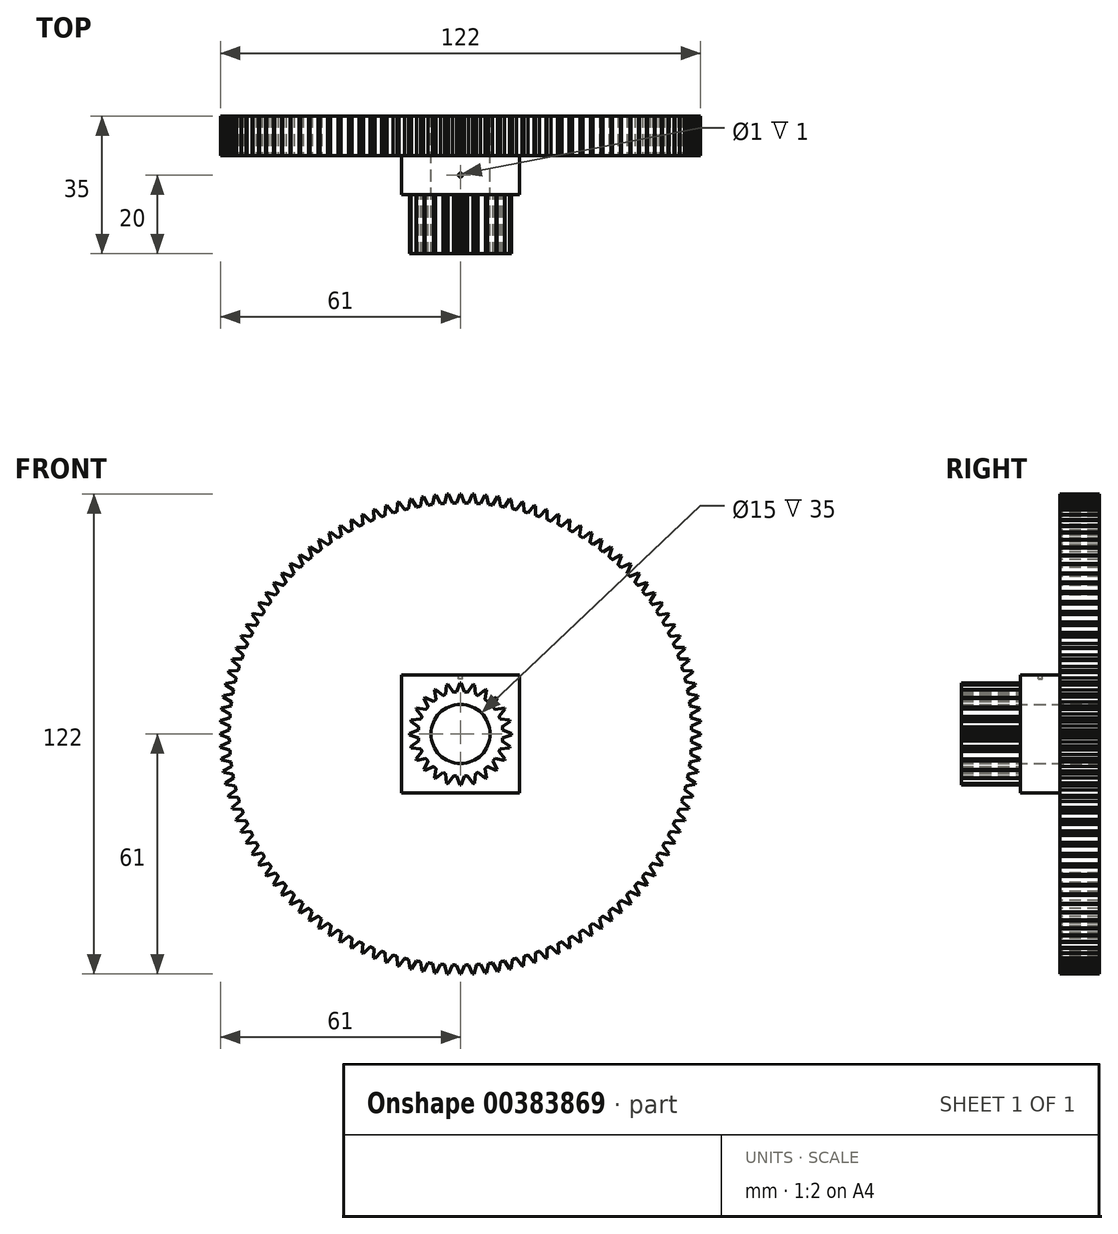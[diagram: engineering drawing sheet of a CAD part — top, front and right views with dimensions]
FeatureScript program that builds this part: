
annotation { "Feature Type Name" : "Feature", "Feature Type Description" : "" }
export const myFeature = defineFeature(function(context is Context, id is Id, definition is map)
    precondition{}
    {
        {
            var Q0;
            Q0=qCreatedBy(makeId("Front.planeOp"),FACE);
            var sketch = newSketch(context, id + "F0", { "sketchPlane" : qUnion([Q0])});
            skCircle(sketch, "E0", {"center": v(0, 0) * mm, "radius": 7.5 * mm});
            skCircle(sketch, "E1", {"center": v(0, 0) * mm, "radius": 10.75 * mm});
            skCircle(sketch, "E2", {"center": v(0, 0) * mm, "radius": 13 * mm, "construction": true});
            skLineSegment(sketch, "E3", {"start": v(-1.02, 10.7) * mm, "end": v(-0.19, 13) * mm});
            skLineSegment(sketch, "E4", {"start": v(-0.19, 13) * mm, "end": v(0, 13) * mm});
            skLineSegment(sketch, "E5", {"start": v(-1.02, 10.7) * mm, "end": v(-1.02, 13.91) * mm, "construction": true});
            skLineSegment(sketch, "E6.MirrorCS", {"start": v(0.19, 13) * mm, "end": v(0, 13) * mm});
            skLineSegment(sketch, "E7.MirrorCS", {"start": v(1.02, 10.7) * mm, "end": v(0.19, 13) * mm});
            skLineSegment(sketch, "E8.1.0", {"start": v(-3.76, 10.07) * mm, "end": v(-3.55, 12.5) * mm});
            skLineSegment(sketch, "E8.1.1", {"start": v(-3.55, 12.5) * mm, "end": v(-3.36, 12.56) * mm});
            skLineSegment(sketch, "E8.1.2", {"start": v(-3.18, 12.6) * mm, "end": v(-3.36, 12.56) * mm});
            skLineSegment(sketch, "E8.1.3", {"start": v(-1.78, 10.6) * mm, "end": v(-3.18, 12.6) * mm});
            skLineSegment(sketch, "E8.2.0", {"start": v(-6.24, 8.76) * mm, "end": v(-6.66, 11.16) * mm});
            skLineSegment(sketch, "E8.2.1", {"start": v(-6.66, 11.16) * mm, "end": v(-6.5, 11.26) * mm});
            skLineSegment(sketch, "E8.2.2", {"start": v(-6.34, 11.35) * mm, "end": v(-6.5, 11.26) * mm});
            skLineSegment(sketch, "E8.2.3", {"start": v(-4.46, 9.78) * mm, "end": v(-6.34, 11.35) * mm});
            skLineSegment(sketch, "E8.3.0", {"start": v(-8.3, 6.84) * mm, "end": v(-9.32, 9.06) * mm});
            skLineSegment(sketch, "E8.3.1", {"start": v(-9.32, 9.06) * mm, "end": v(-9.2, 9.2) * mm});
            skLineSegment(sketch, "E8.3.2", {"start": v(-9.06, 9.32) * mm, "end": v(-9.2, 9.2) * mm});
            skLineSegment(sketch, "E8.3.3", {"start": v(-6.84, 8.3) * mm, "end": v(-9.06, 9.32) * mm});
            skLineSegment(sketch, "E8.4.0", {"start": v(-9.78, 4.46) * mm, "end": v(-11.35, 6.34) * mm});
            skLineSegment(sketch, "E8.4.1", {"start": v(-11.35, 6.34) * mm, "end": v(-11.26, 6.5) * mm});
            skLineSegment(sketch, "E8.4.2", {"start": v(-11.16, 6.66) * mm, "end": v(-11.26, 6.5) * mm});
            skLineSegment(sketch, "E8.4.3", {"start": v(-8.76, 6.24) * mm, "end": v(-11.16, 6.66) * mm});
            skLineSegment(sketch, "E8.5.0", {"start": v(-10.6, 1.78) * mm, "end": v(-12.6, 3.18) * mm});
            skLineSegment(sketch, "E8.5.1", {"start": v(-12.6, 3.18) * mm, "end": v(-12.56, 3.36) * mm});
            skLineSegment(sketch, "E8.5.2", {"start": v(-12.5, 3.55) * mm, "end": v(-12.56, 3.36) * mm});
            skLineSegment(sketch, "E8.5.3", {"start": v(-10.07, 3.76) * mm, "end": v(-12.5, 3.55) * mm});
            skLineSegment(sketch, "E8.6.0", {"start": v(-10.7, -1.02) * mm, "end": v(-13, -0.19) * mm});
            skLineSegment(sketch, "E8.6.1", {"start": v(-13, -0.19) * mm, "end": v(-13, 0) * mm});
            skLineSegment(sketch, "E8.6.2", {"start": v(-13, 0.19) * mm, "end": v(-13, 0) * mm});
            skLineSegment(sketch, "E8.6.3", {"start": v(-10.7, 1.02) * mm, "end": v(-13, 0.19) * mm});
            skLineSegment(sketch, "E8.7.0", {"start": v(-10.07, -3.76) * mm, "end": v(-12.5, -3.55) * mm});
            skLineSegment(sketch, "E8.7.1", {"start": v(-12.5, -3.55) * mm, "end": v(-12.56, -3.36) * mm});
            skLineSegment(sketch, "E8.7.2", {"start": v(-12.6, -3.18) * mm, "end": v(-12.56, -3.36) * mm});
            skLineSegment(sketch, "E8.7.3", {"start": v(-10.6, -1.78) * mm, "end": v(-12.6, -3.18) * mm});
            skLineSegment(sketch, "E8.8.0", {"start": v(-8.76, -6.24) * mm, "end": v(-11.16, -6.66) * mm});
            skLineSegment(sketch, "E8.8.1", {"start": v(-11.16, -6.66) * mm, "end": v(-11.26, -6.5) * mm});
            skLineSegment(sketch, "E8.8.2", {"start": v(-11.35, -6.34) * mm, "end": v(-11.26, -6.5) * mm});
            skLineSegment(sketch, "E8.8.3", {"start": v(-9.78, -4.46) * mm, "end": v(-11.35, -6.34) * mm});
            skLineSegment(sketch, "E8.9.0", {"start": v(-6.84, -8.3) * mm, "end": v(-9.06, -9.32) * mm});
            skLineSegment(sketch, "E8.9.1", {"start": v(-9.06, -9.32) * mm, "end": v(-9.2, -9.2) * mm});
            skLineSegment(sketch, "E8.9.2", {"start": v(-9.32, -9.06) * mm, "end": v(-9.2, -9.2) * mm});
            skLineSegment(sketch, "E8.9.3", {"start": v(-8.3, -6.84) * mm, "end": v(-9.32, -9.06) * mm});
            skLineSegment(sketch, "E8.10.0", {"start": v(-4.46, -9.78) * mm, "end": v(-6.34, -11.35) * mm});
            skLineSegment(sketch, "E8.10.1", {"start": v(-6.34, -11.35) * mm, "end": v(-6.5, -11.26) * mm});
            skLineSegment(sketch, "E8.10.2", {"start": v(-6.66, -11.16) * mm, "end": v(-6.5, -11.26) * mm});
            skLineSegment(sketch, "E8.10.3", {"start": v(-6.24, -8.76) * mm, "end": v(-6.66, -11.16) * mm});
            skLineSegment(sketch, "E8.11.0", {"start": v(-1.78, -10.6) * mm, "end": v(-3.18, -12.6) * mm});
            skLineSegment(sketch, "E8.11.1", {"start": v(-3.18, -12.6) * mm, "end": v(-3.36, -12.56) * mm});
            skLineSegment(sketch, "E8.11.2", {"start": v(-3.55, -12.5) * mm, "end": v(-3.36, -12.56) * mm});
            skLineSegment(sketch, "E8.11.3", {"start": v(-3.76, -10.07) * mm, "end": v(-3.55, -12.5) * mm});
            skLineSegment(sketch, "E9.1.12.0", {"start": v(1.02, -10.7) * mm, "end": v(0.19, -13) * mm});
            skLineSegment(sketch, "E9.3.12.0", {"start": v(0.19, -13) * mm, "end": v(0, -13) * mm});
            skLineSegment(sketch, "E9.6.12.0", {"start": v(-0.19, -13) * mm, "end": v(0, -13) * mm});
            skLineSegment(sketch, "E9.9.12.0", {"start": v(-1.02, -10.7) * mm, "end": v(-0.19, -13) * mm});
            skLineSegment(sketch, "E9.1.13.0", {"start": v(3.76, -10.07) * mm, "end": v(3.55, -12.5) * mm});
            skLineSegment(sketch, "E9.3.13.0", {"start": v(3.55, -12.5) * mm, "end": v(3.36, -12.56) * mm});
            skLineSegment(sketch, "E9.6.13.0", {"start": v(3.18, -12.6) * mm, "end": v(3.36, -12.56) * mm});
            skLineSegment(sketch, "E9.9.13.0", {"start": v(1.78, -10.6) * mm, "end": v(3.18, -12.6) * mm});
            skLineSegment(sketch, "E9.1.14.0", {"start": v(6.24, -8.76) * mm, "end": v(6.66, -11.16) * mm});
            skLineSegment(sketch, "E9.3.14.0", {"start": v(6.66, -11.16) * mm, "end": v(6.5, -11.26) * mm});
            skLineSegment(sketch, "E9.6.14.0", {"start": v(6.34, -11.35) * mm, "end": v(6.5, -11.26) * mm});
            skLineSegment(sketch, "E9.9.14.0", {"start": v(4.46, -9.78) * mm, "end": v(6.34, -11.35) * mm});
            skLineSegment(sketch, "E9.1.15.0", {"start": v(8.3, -6.84) * mm, "end": v(9.32, -9.06) * mm});
            skLineSegment(sketch, "E9.3.15.0", {"start": v(9.32, -9.06) * mm, "end": v(9.2, -9.2) * mm});
            skLineSegment(sketch, "E9.6.15.0", {"start": v(9.06, -9.32) * mm, "end": v(9.2, -9.2) * mm});
            skLineSegment(sketch, "E9.9.15.0", {"start": v(6.84, -8.3) * mm, "end": v(9.06, -9.32) * mm});
            skLineSegment(sketch, "E9.1.16.0", {"start": v(9.78, -4.46) * mm, "end": v(11.35, -6.34) * mm});
            skLineSegment(sketch, "E9.3.16.0", {"start": v(11.35, -6.34) * mm, "end": v(11.26, -6.5) * mm});
            skLineSegment(sketch, "E9.6.16.0", {"start": v(11.16, -6.66) * mm, "end": v(11.26, -6.5) * mm});
            skLineSegment(sketch, "E9.9.16.0", {"start": v(8.76, -6.24) * mm, "end": v(11.16, -6.66) * mm});
            skLineSegment(sketch, "E9.1.17.0", {"start": v(10.6, -1.78) * mm, "end": v(12.6, -3.18) * mm});
            skLineSegment(sketch, "E9.3.17.0", {"start": v(12.6, -3.18) * mm, "end": v(12.56, -3.36) * mm});
            skLineSegment(sketch, "E9.6.17.0", {"start": v(12.5, -3.55) * mm, "end": v(12.56, -3.36) * mm});
            skLineSegment(sketch, "E9.9.17.0", {"start": v(10.07, -3.76) * mm, "end": v(12.5, -3.55) * mm});
            skLineSegment(sketch, "E9.1.18.0", {"start": v(10.7, 1.02) * mm, "end": v(13, 0.19) * mm});
            skLineSegment(sketch, "E9.3.18.0", {"start": v(13, 0.19) * mm, "end": v(13, 0) * mm});
            skLineSegment(sketch, "E9.6.18.0", {"start": v(13, -0.19) * mm, "end": v(13, 0) * mm});
            skLineSegment(sketch, "E9.9.18.0", {"start": v(10.7, -1.02) * mm, "end": v(13, -0.19) * mm});
            skLineSegment(sketch, "E9.1.19.0", {"start": v(10.07, 3.76) * mm, "end": v(12.5, 3.55) * mm});
            skLineSegment(sketch, "E9.3.19.0", {"start": v(12.5, 3.55) * mm, "end": v(12.56, 3.36) * mm});
            skLineSegment(sketch, "E9.6.19.0", {"start": v(12.6, 3.18) * mm, "end": v(12.56, 3.36) * mm});
            skLineSegment(sketch, "E9.9.19.0", {"start": v(10.6, 1.78) * mm, "end": v(12.6, 3.18) * mm});
            skLineSegment(sketch, "E9.1.20.0", {"start": v(8.76, 6.24) * mm, "end": v(11.16, 6.66) * mm});
            skLineSegment(sketch, "E9.3.20.0", {"start": v(11.16, 6.66) * mm, "end": v(11.26, 6.5) * mm});
            skLineSegment(sketch, "E9.6.20.0", {"start": v(11.35, 6.34) * mm, "end": v(11.26, 6.5) * mm});
            skLineSegment(sketch, "E9.9.20.0", {"start": v(9.78, 4.46) * mm, "end": v(11.35, 6.34) * mm});
            skLineSegment(sketch, "E9.1.21.0", {"start": v(6.84, 8.3) * mm, "end": v(9.06, 9.32) * mm});
            skLineSegment(sketch, "E9.3.21.0", {"start": v(9.06, 9.32) * mm, "end": v(9.2, 9.2) * mm});
            skLineSegment(sketch, "E9.6.21.0", {"start": v(9.32, 9.06) * mm, "end": v(9.2, 9.2) * mm});
            skLineSegment(sketch, "E9.9.21.0", {"start": v(8.3, 6.84) * mm, "end": v(9.32, 9.06) * mm});
            skLineSegment(sketch, "E9.1.22.0", {"start": v(4.46, 9.78) * mm, "end": v(6.34, 11.35) * mm});
            skLineSegment(sketch, "E9.3.22.0", {"start": v(6.34, 11.35) * mm, "end": v(6.5, 11.26) * mm});
            skLineSegment(sketch, "E9.6.22.0", {"start": v(6.66, 11.16) * mm, "end": v(6.5, 11.26) * mm});
            skLineSegment(sketch, "E9.9.22.0", {"start": v(6.24, 8.76) * mm, "end": v(6.66, 11.16) * mm});
            skLineSegment(sketch, "E9.1.23.0", {"start": v(1.78, 10.6) * mm, "end": v(3.18, 12.6) * mm});
            skLineSegment(sketch, "E9.3.23.0", {"start": v(3.18, 12.6) * mm, "end": v(3.36, 12.56) * mm});
            skLineSegment(sketch, "E9.6.23.0", {"start": v(3.55, 12.5) * mm, "end": v(3.36, 12.56) * mm});
            skLineSegment(sketch, "E9.9.23.0", {"start": v(3.76, 10.07) * mm, "end": v(3.55, 12.5) * mm});
            skSolve(sketch);
        }
        {
            var Q0;
            Q0=qSketchRegion(id+"F0",true);
            extrude(context, id + "F1", {"entities" : qUnion([Q0]), "depth" : 15 * mm});
        }
        {
            var Q0;
            Q0=qCreatedBy(makeId("Front.planeOp"),FACE);
            var sketch = newSketch(context, id + "F2", { "sketchPlane" : qUnion([Q0])});
            skCircle(sketch, "E10", {"center": v(0, 0) * mm, "radius": 7.5 * mm});
            skLineSegment(sketch, "E11.bottom", {"start": v(-15, -15) * mm, "end": v(15, -15) * mm});
            skLineSegment(sketch, "E11.top", {"start": v(-15, 15) * mm, "end": v(15, 15) * mm});
            skLineSegment(sketch, "E11.left", {"start": v(-15, -15) * mm, "end": v(-15, 15) * mm});
            skLineSegment(sketch, "E11.right", {"start": v(15, -15) * mm, "end": v(15, 15) * mm});
            skSolve(sketch);
        }
        {
            var Q0;
            Q0 = qSketchRegion(id + "F2", true);
            extrude(context, id + "F3", {"entities" : qUnion([Q0]), "operationType" : NewBodyOperationType.ADD, "depth" : -10 * mm});
        }
        {
            var Q0;
            Q0=makeQuery(id+"F3.opExtrude","CAP_FACE",FACE,{"disambiguationData":[OSD([sQuery(id+"F2.wireOp",EDGE,"Zh5lLQ9h-1iR5-KiPg-C2Wr-JR3NM9Zv75rL"),sQuery(id+"F2.wireOp",EDGE,"E10")])],"isStart":false});
            var sketch = newSketch(context, id + "F4", { "sketchPlane" : qUnion([Q0])});
            skCircle(sketch, "E12", {"center": v(0, 0) * mm, "radius": 58.75 * mm});
            skCircle(sketch, "E13", {"center": v(0, 0) * mm, "radius": 61 * mm, "construction": true});
            skLineSegment(sketch, "E14", {"start": v(-1, 58.74) * mm, "end": v(-1, 64.16) * mm, "construction": true});
            skLineSegment(sketch, "E15", {"start": v(-1, 58.74) * mm, "end": v(-0.19, 61) * mm});
            skLineSegment(sketch, "E16", {"start": v(-0.19, 61) * mm, "end": v(0, 61) * mm});
            skLineSegment(sketch, "E17.MirrorCS", {"start": v(0.19, 61) * mm, "end": v(0, 61) * mm});
            skLineSegment(sketch, "E18.MirrorCS", {"start": v(1, 58.74) * mm, "end": v(0.19, 61) * mm});
            skLineSegment(sketch, "E19.1.0", {"start": v(-4.08, 58.6) * mm, "end": v(-3.38, 60.9) * mm});
            skLineSegment(sketch, "E19.1.1", {"start": v(-3.38, 60.9) * mm, "end": v(-3.2, 60.92) * mm});
            skLineSegment(sketch, "E19.1.2", {"start": v(-3, 60.93) * mm, "end": v(-3.2, 60.92) * mm});
            skLineSegment(sketch, "E19.1.3", {"start": v(-2.07, 58.71) * mm, "end": v(-3, 60.93) * mm});
            skLineSegment(sketch, "E19.2.0", {"start": v(-7.14, 58.31) * mm, "end": v(-6.56, 60.65) * mm});
            skLineSegment(sketch, "E19.2.1", {"start": v(-6.56, 60.65) * mm, "end": v(-6.38, 60.67) * mm});
            skLineSegment(sketch, "E19.2.2", {"start": v(-6.19, 60.69) * mm, "end": v(-6.38, 60.67) * mm});
            skLineSegment(sketch, "E19.2.3", {"start": v(-5.14, 58.53) * mm, "end": v(-6.19, 60.69) * mm});
            skLineSegment(sketch, "E19.3.0", {"start": v(-10.19, 57.86) * mm, "end": v(-9.73, 60.22) * mm});
            skLineSegment(sketch, "E19.3.1", {"start": v(-9.73, 60.22) * mm, "end": v(-9.54, 60.25) * mm});
            skLineSegment(sketch, "E19.3.2", {"start": v(-9.36, 60.28) * mm, "end": v(-9.54, 60.25) * mm});
            skLineSegment(sketch, "E19.3.3", {"start": v(-8.2, 58.18) * mm, "end": v(-9.36, 60.28) * mm});
            skLineSegment(sketch, "E19.4.0", {"start": v(-13.2, 57.25) * mm, "end": v(-12.87, 59.63) * mm});
            skLineSegment(sketch, "E19.4.1", {"start": v(-12.87, 59.63) * mm, "end": v(-12.68, 59.67) * mm});
            skLineSegment(sketch, "E19.4.2", {"start": v(-12.5, 59.7) * mm, "end": v(-12.68, 59.67) * mm});
            skLineSegment(sketch, "E19.4.3", {"start": v(-11.23, 57.67) * mm, "end": v(-12.5, 59.7) * mm});
            skLineSegment(sketch, "E19.5.0", {"start": v(-16.18, 56.48) * mm, "end": v(-15.97, 58.87) * mm});
            skLineSegment(sketch, "E19.5.1", {"start": v(-15.97, 58.87) * mm, "end": v(-15.79, 58.92) * mm});
            skLineSegment(sketch, "E19.5.2", {"start": v(-15.6, 58.97) * mm, "end": v(-15.79, 58.92) * mm});
            skLineSegment(sketch, "E19.5.3", {"start": v(-14.23, 57) * mm, "end": v(-15.6, 58.97) * mm});
            skLineSegment(sketch, "E19.6.0", {"start": v(-19.11, 55.55) * mm, "end": v(-19.03, 57.96) * mm});
            skLineSegment(sketch, "E19.6.1", {"start": v(-19.03, 57.96) * mm, "end": v(-18.85, 58.01) * mm});
            skLineSegment(sketch, "E19.6.2", {"start": v(-18.67, 58.07) * mm, "end": v(-18.85, 58.01) * mm});
            skLineSegment(sketch, "E19.6.3", {"start": v(-17.2, 56.18) * mm, "end": v(-18.67, 58.07) * mm});
            skLineSegment(sketch, "E19.7.0", {"start": v(-22, 54.48) * mm, "end": v(-22.04, 56.88) * mm});
            skLineSegment(sketch, "E19.7.1", {"start": v(-22.04, 56.88) * mm, "end": v(-21.86, 56.95) * mm});
            skLineSegment(sketch, "E19.7.2", {"start": v(-21.69, 57.02) * mm, "end": v(-21.86, 56.95) * mm});
            skLineSegment(sketch, "E19.7.3", {"start": v(-20.1, 55.2) * mm, "end": v(-21.69, 57.02) * mm});
            skLineSegment(sketch, "E19.8.0", {"start": v(-24.81, 53.25) * mm, "end": v(-24.98, 55.65) * mm});
            skLineSegment(sketch, "E19.8.1", {"start": v(-24.98, 55.65) * mm, "end": v(-24.81, 55.73) * mm});
            skLineSegment(sketch, "E19.8.2", {"start": v(-24.64, 55.8) * mm, "end": v(-24.81, 55.73) * mm});
            skLineSegment(sketch, "E19.8.3", {"start": v(-22.97, 54.07) * mm, "end": v(-24.64, 55.8) * mm});
            skLineSegment(sketch, "E19.9.0", {"start": v(-27.57, 51.88) * mm, "end": v(-27.86, 54.27) * mm});
            skLineSegment(sketch, "E19.9.1", {"start": v(-27.86, 54.27) * mm, "end": v(-27.7, 54.35) * mm});
            skLineSegment(sketch, "E19.9.2", {"start": v(-27.53, 54.44) * mm, "end": v(-27.7, 54.35) * mm});
            skLineSegment(sketch, "E19.9.3", {"start": v(-25.77, 52.8) * mm, "end": v(-27.53, 54.44) * mm});
            skLineSegment(sketch, "E19.10.0", {"start": v(-30.24, 50.37) * mm, "end": v(-30.66, 52.73) * mm});
            skLineSegment(sketch, "E19.10.1", {"start": v(-30.66, 52.73) * mm, "end": v(-30.5, 52.83) * mm});
            skLineSegment(sketch, "E19.10.2", {"start": v(-30.34, 52.92) * mm, "end": v(-30.5, 52.83) * mm});
            skLineSegment(sketch, "E19.10.3", {"start": v(-28.5, 51.38) * mm, "end": v(-30.34, 52.92) * mm});
            skLineSegment(sketch, "E19.11.0", {"start": v(-32.84, 48.71) * mm, "end": v(-33.38, 51.06) * mm});
            skLineSegment(sketch, "E19.11.1", {"start": v(-33.38, 51.06) * mm, "end": v(-33.22, 51.16) * mm});
            skLineSegment(sketch, "E19.11.2", {"start": v(-33.07, 51.26) * mm, "end": v(-33.22, 51.16) * mm});
            skLineSegment(sketch, "E19.11.3", {"start": v(-31.15, 49.81) * mm, "end": v(-33.07, 51.26) * mm});
            skLineSegment(sketch, "E19.12.0", {"start": v(-35.34, 46.93) * mm, "end": v(-36, 49.24) * mm});
            skLineSegment(sketch, "E19.12.1", {"start": v(-36, 49.24) * mm, "end": v(-35.85, 49.35) * mm});
            skLineSegment(sketch, "E19.12.2", {"start": v(-35.7, 49.46) * mm, "end": v(-35.85, 49.35) * mm});
            skLineSegment(sketch, "E19.12.3", {"start": v(-33.71, 48.12) * mm, "end": v(-35.7, 49.46) * mm});
            skLineSegment(sketch, "E19.13.0", {"start": v(-37.75, 45.02) * mm, "end": v(-38.53, 47.29) * mm});
            skLineSegment(sketch, "E19.13.1", {"start": v(-38.53, 47.29) * mm, "end": v(-38.39, 47.4) * mm});
            skLineSegment(sketch, "E19.13.2", {"start": v(-38.24, 47.52) * mm, "end": v(-38.39, 47.4) * mm});
            skLineSegment(sketch, "E19.13.3", {"start": v(-36.18, 46.29) * mm, "end": v(-38.24, 47.52) * mm});
            skLineSegment(sketch, "E19.14.0", {"start": v(-40.06, 42.98) * mm, "end": v(-40.96, 45.2) * mm});
            skLineSegment(sketch, "E19.14.1", {"start": v(-40.96, 45.2) * mm, "end": v(-40.82, 45.33) * mm});
            skLineSegment(sketch, "E19.14.2", {"start": v(-40.68, 45.46) * mm, "end": v(-40.82, 45.33) * mm});
            skLineSegment(sketch, "E19.14.3", {"start": v(-38.56, 44.33) * mm, "end": v(-40.68, 45.46) * mm});
            skLineSegment(sketch, "E19.15.0", {"start": v(-42.25, 40.82) * mm, "end": v(-43.27, 43) * mm});
            skLineSegment(sketch, "E19.15.1", {"start": v(-43.27, 43) * mm, "end": v(-43.13, 43.13) * mm});
            skLineSegment(sketch, "E19.15.2", {"start": v(-43, 43.27) * mm, "end": v(-43.13, 43.13) * mm});
            skLineSegment(sketch, "E19.15.3", {"start": v(-40.82, 42.25) * mm, "end": v(-43, 43.27) * mm});
            skLineSegment(sketch, "E19.16.0", {"start": v(-44.33, 38.56) * mm, "end": v(-45.46, 40.68) * mm});
            skLineSegment(sketch, "E19.16.1", {"start": v(-45.46, 40.68) * mm, "end": v(-45.33, 40.82) * mm});
            skLineSegment(sketch, "E19.16.2", {"start": v(-45.2, 40.96) * mm, "end": v(-45.33, 40.82) * mm});
            skLineSegment(sketch, "E19.16.3", {"start": v(-42.98, 40.06) * mm, "end": v(-45.2, 40.96) * mm});
            skLineSegment(sketch, "E19.17.0", {"start": v(-46.29, 36.18) * mm, "end": v(-47.52, 38.24) * mm});
            skLineSegment(sketch, "E19.17.1", {"start": v(-47.52, 38.24) * mm, "end": v(-47.4, 38.39) * mm});
            skLineSegment(sketch, "E19.17.2", {"start": v(-47.29, 38.53) * mm, "end": v(-47.4, 38.39) * mm});
            skLineSegment(sketch, "E19.17.3", {"start": v(-45.02, 37.75) * mm, "end": v(-47.29, 38.53) * mm});
            skLineSegment(sketch, "E19.18.0", {"start": v(-48.12, 33.71) * mm, "end": v(-49.46, 35.7) * mm});
            skLineSegment(sketch, "E19.18.1", {"start": v(-49.46, 35.7) * mm, "end": v(-49.35, 35.85) * mm});
            skLineSegment(sketch, "E19.18.2", {"start": v(-49.24, 36) * mm, "end": v(-49.35, 35.85) * mm});
            skLineSegment(sketch, "E19.18.3", {"start": v(-46.93, 35.34) * mm, "end": v(-49.24, 36) * mm});
            skLineSegment(sketch, "E19.19.0", {"start": v(-49.81, 31.15) * mm, "end": v(-51.26, 33.07) * mm});
            skLineSegment(sketch, "E19.19.1", {"start": v(-51.26, 33.07) * mm, "end": v(-51.16, 33.22) * mm});
            skLineSegment(sketch, "E19.19.2", {"start": v(-51.06, 33.38) * mm, "end": v(-51.16, 33.22) * mm});
            skLineSegment(sketch, "E19.19.3", {"start": v(-48.71, 32.84) * mm, "end": v(-51.06, 33.38) * mm});
            skLineSegment(sketch, "E19.20.0", {"start": v(-51.38, 28.5) * mm, "end": v(-52.92, 30.34) * mm});
            skLineSegment(sketch, "E19.20.1", {"start": v(-52.92, 30.34) * mm, "end": v(-52.83, 30.5) * mm});
            skLineSegment(sketch, "E19.20.2", {"start": v(-52.73, 30.66) * mm, "end": v(-52.83, 30.5) * mm});
            skLineSegment(sketch, "E19.20.3", {"start": v(-50.37, 30.24) * mm, "end": v(-52.73, 30.66) * mm});
            skLineSegment(sketch, "E19.21.0", {"start": v(-52.8, 25.77) * mm, "end": v(-54.44, 27.53) * mm});
            skLineSegment(sketch, "E19.21.1", {"start": v(-54.44, 27.53) * mm, "end": v(-54.35, 27.7) * mm});
            skLineSegment(sketch, "E19.21.2", {"start": v(-54.27, 27.86) * mm, "end": v(-54.35, 27.7) * mm});
            skLineSegment(sketch, "E19.21.3", {"start": v(-51.88, 27.57) * mm, "end": v(-54.27, 27.86) * mm});
            skLineSegment(sketch, "E19.22.0", {"start": v(-54.07, 22.97) * mm, "end": v(-55.8, 24.64) * mm});
            skLineSegment(sketch, "E19.22.1", {"start": v(-55.8, 24.64) * mm, "end": v(-55.73, 24.81) * mm});
            skLineSegment(sketch, "E19.22.2", {"start": v(-55.65, 24.98) * mm, "end": v(-55.73, 24.81) * mm});
            skLineSegment(sketch, "E19.22.3", {"start": v(-53.25, 24.81) * mm, "end": v(-55.65, 24.98) * mm});
            skLineSegment(sketch, "E19.23.0", {"start": v(-55.2, 20.1) * mm, "end": v(-57.02, 21.69) * mm});
            skLineSegment(sketch, "E19.23.1", {"start": v(-57.02, 21.69) * mm, "end": v(-56.95, 21.86) * mm});
            skLineSegment(sketch, "E19.23.2", {"start": v(-56.88, 22.04) * mm, "end": v(-56.95, 21.86) * mm});
            skLineSegment(sketch, "E19.23.3", {"start": v(-54.48, 22) * mm, "end": v(-56.88, 22.04) * mm});
            skLineSegment(sketch, "E19.24.0", {"start": v(-56.18, 17.2) * mm, "end": v(-58.07, 18.67) * mm});
            skLineSegment(sketch, "E19.24.1", {"start": v(-58.07, 18.67) * mm, "end": v(-58.01, 18.85) * mm});
            skLineSegment(sketch, "E19.24.2", {"start": v(-57.96, 19.03) * mm, "end": v(-58.01, 18.85) * mm});
            skLineSegment(sketch, "E19.24.3", {"start": v(-55.55, 19.11) * mm, "end": v(-57.96, 19.03) * mm});
            skLineSegment(sketch, "E19.25.0", {"start": v(-57, 14.23) * mm, "end": v(-58.97, 15.6) * mm});
            skLineSegment(sketch, "E19.25.1", {"start": v(-58.97, 15.6) * mm, "end": v(-58.92, 15.79) * mm});
            skLineSegment(sketch, "E19.25.2", {"start": v(-58.87, 15.97) * mm, "end": v(-58.92, 15.79) * mm});
            skLineSegment(sketch, "E19.25.3", {"start": v(-56.48, 16.18) * mm, "end": v(-58.87, 15.97) * mm});
            skLineSegment(sketch, "E19.26.0", {"start": v(-57.67, 11.23) * mm, "end": v(-59.7, 12.5) * mm});
            skLineSegment(sketch, "E19.26.1", {"start": v(-59.7, 12.5) * mm, "end": v(-59.67, 12.68) * mm});
            skLineSegment(sketch, "E19.26.2", {"start": v(-59.63, 12.87) * mm, "end": v(-59.67, 12.68) * mm});
            skLineSegment(sketch, "E19.26.3", {"start": v(-57.25, 13.2) * mm, "end": v(-59.63, 12.87) * mm});
            skLineSegment(sketch, "E19.27.0", {"start": v(-58.18, 8.2) * mm, "end": v(-60.28, 9.36) * mm});
            skLineSegment(sketch, "E19.27.1", {"start": v(-60.28, 9.36) * mm, "end": v(-60.25, 9.54) * mm});
            skLineSegment(sketch, "E19.27.2", {"start": v(-60.22, 9.73) * mm, "end": v(-60.25, 9.54) * mm});
            skLineSegment(sketch, "E19.27.3", {"start": v(-57.86, 10.19) * mm, "end": v(-60.22, 9.73) * mm});
            skLineSegment(sketch, "E19.28.0", {"start": v(-58.53, 5.14) * mm, "end": v(-60.69, 6.19) * mm});
            skLineSegment(sketch, "E19.28.1", {"start": v(-60.69, 6.19) * mm, "end": v(-60.67, 6.38) * mm});
            skLineSegment(sketch, "E19.28.2", {"start": v(-60.65, 6.56) * mm, "end": v(-60.67, 6.38) * mm});
            skLineSegment(sketch, "E19.28.3", {"start": v(-58.31, 7.14) * mm, "end": v(-60.65, 6.56) * mm});
            skLineSegment(sketch, "E19.29.0", {"start": v(-58.71, 2.07) * mm, "end": v(-60.93, 3) * mm});
            skLineSegment(sketch, "E19.29.1", {"start": v(-60.93, 3) * mm, "end": v(-60.92, 3.2) * mm});
            skLineSegment(sketch, "E19.29.2", {"start": v(-60.9, 3.38) * mm, "end": v(-60.92, 3.2) * mm});
            skLineSegment(sketch, "E19.29.3", {"start": v(-58.6, 4.08) * mm, "end": v(-60.9, 3.38) * mm});
            skLineSegment(sketch, "E19.30.0", {"start": v(-58.74, -1) * mm, "end": v(-61, -0.19) * mm});
            skLineSegment(sketch, "E19.30.1", {"start": v(-61, -0.19) * mm, "end": v(-61, 0) * mm});
            skLineSegment(sketch, "E19.30.2", {"start": v(-61, 0.19) * mm, "end": v(-61, 0) * mm});
            skLineSegment(sketch, "E19.30.3", {"start": v(-58.74, 1) * mm, "end": v(-61, 0.19) * mm});
            skLineSegment(sketch, "E19.31.0", {"start": v(-58.6, -4.08) * mm, "end": v(-60.9, -3.38) * mm});
            skLineSegment(sketch, "E19.31.1", {"start": v(-60.9, -3.38) * mm, "end": v(-60.92, -3.2) * mm});
            skLineSegment(sketch, "E19.31.2", {"start": v(-60.93, -3) * mm, "end": v(-60.92, -3.2) * mm});
            skLineSegment(sketch, "E19.31.3", {"start": v(-58.71, -2.07) * mm, "end": v(-60.93, -3) * mm});
            skLineSegment(sketch, "E19.32.0", {"start": v(-58.31, -7.14) * mm, "end": v(-60.65, -6.56) * mm});
            skLineSegment(sketch, "E19.32.1", {"start": v(-60.65, -6.56) * mm, "end": v(-60.67, -6.38) * mm});
            skLineSegment(sketch, "E19.32.2", {"start": v(-60.69, -6.19) * mm, "end": v(-60.67, -6.38) * mm});
            skLineSegment(sketch, "E19.32.3", {"start": v(-58.53, -5.14) * mm, "end": v(-60.69, -6.19) * mm});
            skLineSegment(sketch, "E19.33.0", {"start": v(-57.86, -10.19) * mm, "end": v(-60.22, -9.73) * mm});
            skLineSegment(sketch, "E19.33.1", {"start": v(-60.22, -9.73) * mm, "end": v(-60.25, -9.54) * mm});
            skLineSegment(sketch, "E19.33.2", {"start": v(-60.28, -9.36) * mm, "end": v(-60.25, -9.54) * mm});
            skLineSegment(sketch, "E19.33.3", {"start": v(-58.18, -8.2) * mm, "end": v(-60.28, -9.36) * mm});
            skLineSegment(sketch, "E19.34.0", {"start": v(-57.25, -13.2) * mm, "end": v(-59.63, -12.87) * mm});
            skLineSegment(sketch, "E19.34.1", {"start": v(-59.63, -12.87) * mm, "end": v(-59.67, -12.68) * mm});
            skLineSegment(sketch, "E19.34.2", {"start": v(-59.7, -12.5) * mm, "end": v(-59.67, -12.68) * mm});
            skLineSegment(sketch, "E19.34.3", {"start": v(-57.67, -11.23) * mm, "end": v(-59.7, -12.5) * mm});
            skLineSegment(sketch, "E19.35.0", {"start": v(-56.48, -16.18) * mm, "end": v(-58.87, -15.97) * mm});
            skLineSegment(sketch, "E19.35.1", {"start": v(-58.87, -15.97) * mm, "end": v(-58.92, -15.79) * mm});
            skLineSegment(sketch, "E19.35.2", {"start": v(-58.97, -15.6) * mm, "end": v(-58.92, -15.79) * mm});
            skLineSegment(sketch, "E19.35.3", {"start": v(-57, -14.23) * mm, "end": v(-58.97, -15.6) * mm});
            skLineSegment(sketch, "E19.36.0", {"start": v(-55.55, -19.11) * mm, "end": v(-57.96, -19.03) * mm});
            skLineSegment(sketch, "E19.36.1", {"start": v(-57.96, -19.03) * mm, "end": v(-58.01, -18.85) * mm});
            skLineSegment(sketch, "E19.36.2", {"start": v(-58.07, -18.67) * mm, "end": v(-58.01, -18.85) * mm});
            skLineSegment(sketch, "E19.36.3", {"start": v(-56.18, -17.2) * mm, "end": v(-58.07, -18.67) * mm});
            skLineSegment(sketch, "E19.37.0", {"start": v(-54.48, -22) * mm, "end": v(-56.88, -22.04) * mm});
            skLineSegment(sketch, "E19.37.1", {"start": v(-56.88, -22.04) * mm, "end": v(-56.95, -21.86) * mm});
            skLineSegment(sketch, "E19.37.2", {"start": v(-57.02, -21.69) * mm, "end": v(-56.95, -21.86) * mm});
            skLineSegment(sketch, "E19.37.3", {"start": v(-55.2, -20.1) * mm, "end": v(-57.02, -21.69) * mm});
            skLineSegment(sketch, "E19.38.0", {"start": v(-53.25, -24.81) * mm, "end": v(-55.65, -24.98) * mm});
            skLineSegment(sketch, "E19.38.1", {"start": v(-55.65, -24.98) * mm, "end": v(-55.73, -24.81) * mm});
            skLineSegment(sketch, "E19.38.2", {"start": v(-55.8, -24.64) * mm, "end": v(-55.73, -24.81) * mm});
            skLineSegment(sketch, "E19.38.3", {"start": v(-54.07, -22.97) * mm, "end": v(-55.8, -24.64) * mm});
            skLineSegment(sketch, "E19.39.0", {"start": v(-51.88, -27.57) * mm, "end": v(-54.27, -27.86) * mm});
            skLineSegment(sketch, "E19.39.1", {"start": v(-54.27, -27.86) * mm, "end": v(-54.35, -27.7) * mm});
            skLineSegment(sketch, "E19.39.2", {"start": v(-54.44, -27.53) * mm, "end": v(-54.35, -27.7) * mm});
            skLineSegment(sketch, "E19.39.3", {"start": v(-52.8, -25.77) * mm, "end": v(-54.44, -27.53) * mm});
            skLineSegment(sketch, "E19.40.0", {"start": v(-50.37, -30.24) * mm, "end": v(-52.73, -30.66) * mm});
            skLineSegment(sketch, "E19.40.1", {"start": v(-52.73, -30.66) * mm, "end": v(-52.83, -30.5) * mm});
            skLineSegment(sketch, "E19.40.2", {"start": v(-52.92, -30.34) * mm, "end": v(-52.83, -30.5) * mm});
            skLineSegment(sketch, "E19.40.3", {"start": v(-51.38, -28.5) * mm, "end": v(-52.92, -30.34) * mm});
            skLineSegment(sketch, "E19.41.0", {"start": v(-48.71, -32.84) * mm, "end": v(-51.06, -33.38) * mm});
            skLineSegment(sketch, "E19.41.1", {"start": v(-51.06, -33.38) * mm, "end": v(-51.16, -33.22) * mm});
            skLineSegment(sketch, "E19.41.2", {"start": v(-51.26, -33.07) * mm, "end": v(-51.16, -33.22) * mm});
            skLineSegment(sketch, "E19.41.3", {"start": v(-49.81, -31.15) * mm, "end": v(-51.26, -33.07) * mm});
            skLineSegment(sketch, "E19.42.0", {"start": v(-46.93, -35.34) * mm, "end": v(-49.24, -36) * mm});
            skLineSegment(sketch, "E19.42.1", {"start": v(-49.24, -36) * mm, "end": v(-49.35, -35.85) * mm});
            skLineSegment(sketch, "E19.42.2", {"start": v(-49.46, -35.7) * mm, "end": v(-49.35, -35.85) * mm});
            skLineSegment(sketch, "E19.42.3", {"start": v(-48.12, -33.71) * mm, "end": v(-49.46, -35.7) * mm});
            skLineSegment(sketch, "E19.43.0", {"start": v(-45.02, -37.75) * mm, "end": v(-47.29, -38.53) * mm});
            skLineSegment(sketch, "E19.43.1", {"start": v(-47.29, -38.53) * mm, "end": v(-47.4, -38.39) * mm});
            skLineSegment(sketch, "E19.43.2", {"start": v(-47.52, -38.24) * mm, "end": v(-47.4, -38.39) * mm});
            skLineSegment(sketch, "E19.43.3", {"start": v(-46.29, -36.18) * mm, "end": v(-47.52, -38.24) * mm});
            skLineSegment(sketch, "E19.44.0", {"start": v(-42.98, -40.06) * mm, "end": v(-45.2, -40.96) * mm});
            skLineSegment(sketch, "E19.44.1", {"start": v(-45.2, -40.96) * mm, "end": v(-45.33, -40.82) * mm});
            skLineSegment(sketch, "E19.44.2", {"start": v(-45.46, -40.68) * mm, "end": v(-45.33, -40.82) * mm});
            skLineSegment(sketch, "E19.44.3", {"start": v(-44.33, -38.56) * mm, "end": v(-45.46, -40.68) * mm});
            skLineSegment(sketch, "E19.45.0", {"start": v(-40.82, -42.25) * mm, "end": v(-43, -43.27) * mm});
            skLineSegment(sketch, "E19.45.1", {"start": v(-43, -43.27) * mm, "end": v(-43.13, -43.13) * mm});
            skLineSegment(sketch, "E19.45.2", {"start": v(-43.27, -43) * mm, "end": v(-43.13, -43.13) * mm});
            skLineSegment(sketch, "E19.45.3", {"start": v(-42.25, -40.82) * mm, "end": v(-43.27, -43) * mm});
            skLineSegment(sketch, "E19.46.0", {"start": v(-38.56, -44.33) * mm, "end": v(-40.68, -45.46) * mm});
            skLineSegment(sketch, "E19.46.1", {"start": v(-40.68, -45.46) * mm, "end": v(-40.82, -45.33) * mm});
            skLineSegment(sketch, "E19.46.2", {"start": v(-40.96, -45.2) * mm, "end": v(-40.82, -45.33) * mm});
            skLineSegment(sketch, "E19.46.3", {"start": v(-40.06, -42.98) * mm, "end": v(-40.96, -45.2) * mm});
            skLineSegment(sketch, "E19.47.0", {"start": v(-36.18, -46.29) * mm, "end": v(-38.24, -47.52) * mm});
            skLineSegment(sketch, "E19.47.1", {"start": v(-38.24, -47.52) * mm, "end": v(-38.39, -47.4) * mm});
            skLineSegment(sketch, "E19.47.2", {"start": v(-38.53, -47.29) * mm, "end": v(-38.39, -47.4) * mm});
            skLineSegment(sketch, "E19.47.3", {"start": v(-37.75, -45.02) * mm, "end": v(-38.53, -47.29) * mm});
            skLineSegment(sketch, "E19.48.0", {"start": v(-33.71, -48.12) * mm, "end": v(-35.7, -49.46) * mm});
            skLineSegment(sketch, "E19.48.1", {"start": v(-35.7, -49.46) * mm, "end": v(-35.85, -49.35) * mm});
            skLineSegment(sketch, "E19.48.2", {"start": v(-36, -49.24) * mm, "end": v(-35.85, -49.35) * mm});
            skLineSegment(sketch, "E19.48.3", {"start": v(-35.34, -46.93) * mm, "end": v(-36, -49.24) * mm});
            skLineSegment(sketch, "E19.49.0", {"start": v(-31.15, -49.81) * mm, "end": v(-33.07, -51.26) * mm});
            skLineSegment(sketch, "E19.49.1", {"start": v(-33.07, -51.26) * mm, "end": v(-33.22, -51.16) * mm});
            skLineSegment(sketch, "E19.49.2", {"start": v(-33.38, -51.06) * mm, "end": v(-33.22, -51.16) * mm});
            skLineSegment(sketch, "E19.49.3", {"start": v(-32.84, -48.71) * mm, "end": v(-33.38, -51.06) * mm});
            skLineSegment(sketch, "E19.50.0", {"start": v(-28.5, -51.38) * mm, "end": v(-30.34, -52.92) * mm});
            skLineSegment(sketch, "E19.50.1", {"start": v(-30.34, -52.92) * mm, "end": v(-30.5, -52.83) * mm});
            skLineSegment(sketch, "E19.50.2", {"start": v(-30.66, -52.73) * mm, "end": v(-30.5, -52.83) * mm});
            skLineSegment(sketch, "E19.50.3", {"start": v(-30.24, -50.37) * mm, "end": v(-30.66, -52.73) * mm});
            skLineSegment(sketch, "E19.51.0", {"start": v(-25.77, -52.8) * mm, "end": v(-27.53, -54.44) * mm});
            skLineSegment(sketch, "E19.51.1", {"start": v(-27.53, -54.44) * mm, "end": v(-27.7, -54.35) * mm});
            skLineSegment(sketch, "E19.51.2", {"start": v(-27.86, -54.27) * mm, "end": v(-27.7, -54.35) * mm});
            skLineSegment(sketch, "E19.51.3", {"start": v(-27.57, -51.88) * mm, "end": v(-27.86, -54.27) * mm});
            skLineSegment(sketch, "E19.52.0", {"start": v(-22.97, -54.07) * mm, "end": v(-24.64, -55.8) * mm});
            skLineSegment(sketch, "E19.52.1", {"start": v(-24.64, -55.8) * mm, "end": v(-24.81, -55.73) * mm});
            skLineSegment(sketch, "E19.52.2", {"start": v(-24.98, -55.65) * mm, "end": v(-24.81, -55.73) * mm});
            skLineSegment(sketch, "E19.52.3", {"start": v(-24.81, -53.25) * mm, "end": v(-24.98, -55.65) * mm});
            skLineSegment(sketch, "E19.53.0", {"start": v(-20.1, -55.2) * mm, "end": v(-21.69, -57.02) * mm});
            skLineSegment(sketch, "E19.53.1", {"start": v(-21.69, -57.02) * mm, "end": v(-21.86, -56.95) * mm});
            skLineSegment(sketch, "E19.53.2", {"start": v(-22.04, -56.88) * mm, "end": v(-21.86, -56.95) * mm});
            skLineSegment(sketch, "E19.53.3", {"start": v(-22, -54.48) * mm, "end": v(-22.04, -56.88) * mm});
            skLineSegment(sketch, "E19.54.0", {"start": v(-17.2, -56.18) * mm, "end": v(-18.67, -58.07) * mm});
            skLineSegment(sketch, "E19.54.1", {"start": v(-18.67, -58.07) * mm, "end": v(-18.85, -58.01) * mm});
            skLineSegment(sketch, "E19.54.2", {"start": v(-19.03, -57.96) * mm, "end": v(-18.85, -58.01) * mm});
            skLineSegment(sketch, "E19.54.3", {"start": v(-19.11, -55.55) * mm, "end": v(-19.03, -57.96) * mm});
            skLineSegment(sketch, "E19.55.0", {"start": v(-14.23, -57) * mm, "end": v(-15.6, -58.97) * mm});
            skLineSegment(sketch, "E19.55.1", {"start": v(-15.6, -58.97) * mm, "end": v(-15.79, -58.92) * mm});
            skLineSegment(sketch, "E19.55.2", {"start": v(-15.97, -58.87) * mm, "end": v(-15.79, -58.92) * mm});
            skLineSegment(sketch, "E19.55.3", {"start": v(-16.18, -56.48) * mm, "end": v(-15.97, -58.87) * mm});
            skLineSegment(sketch, "E19.56.0", {"start": v(-11.23, -57.67) * mm, "end": v(-12.5, -59.7) * mm});
            skLineSegment(sketch, "E19.56.1", {"start": v(-12.5, -59.7) * mm, "end": v(-12.68, -59.67) * mm});
            skLineSegment(sketch, "E19.56.2", {"start": v(-12.87, -59.63) * mm, "end": v(-12.68, -59.67) * mm});
            skLineSegment(sketch, "E19.56.3", {"start": v(-13.2, -57.25) * mm, "end": v(-12.87, -59.63) * mm});
            skLineSegment(sketch, "E19.57.0", {"start": v(-8.2, -58.18) * mm, "end": v(-9.36, -60.28) * mm});
            skLineSegment(sketch, "E19.57.1", {"start": v(-9.36, -60.28) * mm, "end": v(-9.54, -60.25) * mm});
            skLineSegment(sketch, "E19.57.2", {"start": v(-9.73, -60.22) * mm, "end": v(-9.54, -60.25) * mm});
            skLineSegment(sketch, "E19.57.3", {"start": v(-10.19, -57.86) * mm, "end": v(-9.73, -60.22) * mm});
            skLineSegment(sketch, "E19.58.0", {"start": v(-5.14, -58.53) * mm, "end": v(-6.19, -60.69) * mm});
            skLineSegment(sketch, "E19.58.1", {"start": v(-6.19, -60.69) * mm, "end": v(-6.38, -60.67) * mm});
            skLineSegment(sketch, "E19.58.2", {"start": v(-6.56, -60.65) * mm, "end": v(-6.38, -60.67) * mm});
            skLineSegment(sketch, "E19.58.3", {"start": v(-7.14, -58.31) * mm, "end": v(-6.56, -60.65) * mm});
            skLineSegment(sketch, "E19.59.0", {"start": v(-2.07, -58.71) * mm, "end": v(-3, -60.93) * mm});
            skLineSegment(sketch, "E19.59.1", {"start": v(-3, -60.93) * mm, "end": v(-3.2, -60.92) * mm});
            skLineSegment(sketch, "E19.59.2", {"start": v(-3.38, -60.9) * mm, "end": v(-3.2, -60.92) * mm});
            skLineSegment(sketch, "E19.59.3", {"start": v(-4.08, -58.6) * mm, "end": v(-3.38, -60.9) * mm});
            skLineSegment(sketch, "E19.60.0", {"start": v(1, -58.74) * mm, "end": v(0.19, -61) * mm});
            skLineSegment(sketch, "E19.60.1", {"start": v(0.19, -61) * mm, "end": v(0, -61) * mm});
            skLineSegment(sketch, "E19.60.2", {"start": v(-0.19, -61) * mm, "end": v(0, -61) * mm});
            skLineSegment(sketch, "E19.60.3", {"start": v(-1, -58.74) * mm, "end": v(-0.19, -61) * mm});
            skLineSegment(sketch, "E19.61.0", {"start": v(4.08, -58.6) * mm, "end": v(3.38, -60.9) * mm});
            skLineSegment(sketch, "E19.61.1", {"start": v(3.38, -60.9) * mm, "end": v(3.2, -60.92) * mm});
            skLineSegment(sketch, "E19.61.2", {"start": v(3, -60.93) * mm, "end": v(3.2, -60.92) * mm});
            skLineSegment(sketch, "E19.61.3", {"start": v(2.07, -58.71) * mm, "end": v(3, -60.93) * mm});
            skLineSegment(sketch, "E19.62.0", {"start": v(7.14, -58.31) * mm, "end": v(6.56, -60.65) * mm});
            skLineSegment(sketch, "E19.62.1", {"start": v(6.56, -60.65) * mm, "end": v(6.38, -60.67) * mm});
            skLineSegment(sketch, "E19.62.2", {"start": v(6.19, -60.69) * mm, "end": v(6.38, -60.67) * mm});
            skLineSegment(sketch, "E19.62.3", {"start": v(5.14, -58.53) * mm, "end": v(6.19, -60.69) * mm});
            skLineSegment(sketch, "E19.63.0", {"start": v(10.19, -57.86) * mm, "end": v(9.73, -60.22) * mm});
            skLineSegment(sketch, "E19.63.1", {"start": v(9.73, -60.22) * mm, "end": v(9.54, -60.25) * mm});
            skLineSegment(sketch, "E19.63.2", {"start": v(9.36, -60.28) * mm, "end": v(9.54, -60.25) * mm});
            skLineSegment(sketch, "E19.63.3", {"start": v(8.2, -58.18) * mm, "end": v(9.36, -60.28) * mm});
            skLineSegment(sketch, "E19.64.0", {"start": v(13.2, -57.25) * mm, "end": v(12.87, -59.63) * mm});
            skLineSegment(sketch, "E19.64.1", {"start": v(12.87, -59.63) * mm, "end": v(12.68, -59.67) * mm});
            skLineSegment(sketch, "E19.64.2", {"start": v(12.5, -59.7) * mm, "end": v(12.68, -59.67) * mm});
            skLineSegment(sketch, "E19.64.3", {"start": v(11.23, -57.67) * mm, "end": v(12.5, -59.7) * mm});
            skLineSegment(sketch, "E19.65.0", {"start": v(16.18, -56.48) * mm, "end": v(15.97, -58.87) * mm});
            skLineSegment(sketch, "E19.65.1", {"start": v(15.97, -58.87) * mm, "end": v(15.79, -58.92) * mm});
            skLineSegment(sketch, "E19.65.2", {"start": v(15.6, -58.97) * mm, "end": v(15.79, -58.92) * mm});
            skLineSegment(sketch, "E19.65.3", {"start": v(14.23, -57) * mm, "end": v(15.6, -58.97) * mm});
            skLineSegment(sketch, "E19.66.0", {"start": v(19.11, -55.55) * mm, "end": v(19.03, -57.96) * mm});
            skLineSegment(sketch, "E19.66.1", {"start": v(19.03, -57.96) * mm, "end": v(18.85, -58.01) * mm});
            skLineSegment(sketch, "E19.66.2", {"start": v(18.67, -58.07) * mm, "end": v(18.85, -58.01) * mm});
            skLineSegment(sketch, "E19.66.3", {"start": v(17.2, -56.18) * mm, "end": v(18.67, -58.07) * mm});
            skLineSegment(sketch, "E19.67.0", {"start": v(22, -54.48) * mm, "end": v(22.04, -56.88) * mm});
            skLineSegment(sketch, "E19.67.1", {"start": v(22.04, -56.88) * mm, "end": v(21.86, -56.95) * mm});
            skLineSegment(sketch, "E19.67.2", {"start": v(21.69, -57.02) * mm, "end": v(21.86, -56.95) * mm});
            skLineSegment(sketch, "E19.67.3", {"start": v(20.1, -55.2) * mm, "end": v(21.69, -57.02) * mm});
            skLineSegment(sketch, "E19.68.0", {"start": v(24.81, -53.25) * mm, "end": v(24.98, -55.65) * mm});
            skLineSegment(sketch, "E19.68.1", {"start": v(24.98, -55.65) * mm, "end": v(24.81, -55.73) * mm});
            skLineSegment(sketch, "E19.68.2", {"start": v(24.64, -55.8) * mm, "end": v(24.81, -55.73) * mm});
            skLineSegment(sketch, "E19.68.3", {"start": v(22.97, -54.07) * mm, "end": v(24.64, -55.8) * mm});
            skLineSegment(sketch, "E19.69.0", {"start": v(27.57, -51.88) * mm, "end": v(27.86, -54.27) * mm});
            skLineSegment(sketch, "E19.69.1", {"start": v(27.86, -54.27) * mm, "end": v(27.7, -54.35) * mm});
            skLineSegment(sketch, "E19.69.2", {"start": v(27.53, -54.44) * mm, "end": v(27.7, -54.35) * mm});
            skLineSegment(sketch, "E19.69.3", {"start": v(25.77, -52.8) * mm, "end": v(27.53, -54.44) * mm});
            skLineSegment(sketch, "E19.70.0", {"start": v(30.24, -50.37) * mm, "end": v(30.66, -52.73) * mm});
            skLineSegment(sketch, "E19.70.1", {"start": v(30.66, -52.73) * mm, "end": v(30.5, -52.83) * mm});
            skLineSegment(sketch, "E19.70.2", {"start": v(30.34, -52.92) * mm, "end": v(30.5, -52.83) * mm});
            skLineSegment(sketch, "E19.70.3", {"start": v(28.5, -51.38) * mm, "end": v(30.34, -52.92) * mm});
            skLineSegment(sketch, "E19.71.0", {"start": v(32.84, -48.71) * mm, "end": v(33.38, -51.06) * mm});
            skLineSegment(sketch, "E19.71.1", {"start": v(33.38, -51.06) * mm, "end": v(33.22, -51.16) * mm});
            skLineSegment(sketch, "E19.71.2", {"start": v(33.07, -51.26) * mm, "end": v(33.22, -51.16) * mm});
            skLineSegment(sketch, "E19.71.3", {"start": v(31.15, -49.81) * mm, "end": v(33.07, -51.26) * mm});
            skLineSegment(sketch, "E19.72.0", {"start": v(35.34, -46.93) * mm, "end": v(36, -49.24) * mm});
            skLineSegment(sketch, "E19.72.1", {"start": v(36, -49.24) * mm, "end": v(35.85, -49.35) * mm});
            skLineSegment(sketch, "E19.72.2", {"start": v(35.7, -49.46) * mm, "end": v(35.85, -49.35) * mm});
            skLineSegment(sketch, "E19.72.3", {"start": v(33.71, -48.12) * mm, "end": v(35.7, -49.46) * mm});
            skLineSegment(sketch, "E19.73.0", {"start": v(37.75, -45.02) * mm, "end": v(38.53, -47.29) * mm});
            skLineSegment(sketch, "E19.73.1", {"start": v(38.53, -47.29) * mm, "end": v(38.39, -47.4) * mm});
            skLineSegment(sketch, "E19.73.2", {"start": v(38.24, -47.52) * mm, "end": v(38.39, -47.4) * mm});
            skLineSegment(sketch, "E19.73.3", {"start": v(36.18, -46.29) * mm, "end": v(38.24, -47.52) * mm});
            skLineSegment(sketch, "E19.74.0", {"start": v(40.06, -42.98) * mm, "end": v(40.96, -45.2) * mm});
            skLineSegment(sketch, "E19.74.1", {"start": v(40.96, -45.2) * mm, "end": v(40.82, -45.33) * mm});
            skLineSegment(sketch, "E19.74.2", {"start": v(40.68, -45.46) * mm, "end": v(40.82, -45.33) * mm});
            skLineSegment(sketch, "E19.74.3", {"start": v(38.56, -44.33) * mm, "end": v(40.68, -45.46) * mm});
            skLineSegment(sketch, "E19.75.0", {"start": v(42.25, -40.82) * mm, "end": v(43.27, -43) * mm});
            skLineSegment(sketch, "E19.75.1", {"start": v(43.27, -43) * mm, "end": v(43.13, -43.13) * mm});
            skLineSegment(sketch, "E19.75.2", {"start": v(43, -43.27) * mm, "end": v(43.13, -43.13) * mm});
            skLineSegment(sketch, "E19.75.3", {"start": v(40.82, -42.25) * mm, "end": v(43, -43.27) * mm});
            skLineSegment(sketch, "E19.76.0", {"start": v(44.33, -38.56) * mm, "end": v(45.46, -40.68) * mm});
            skLineSegment(sketch, "E19.76.1", {"start": v(45.46, -40.68) * mm, "end": v(45.33, -40.82) * mm});
            skLineSegment(sketch, "E19.76.2", {"start": v(45.2, -40.96) * mm, "end": v(45.33, -40.82) * mm});
            skLineSegment(sketch, "E19.76.3", {"start": v(42.98, -40.06) * mm, "end": v(45.2, -40.96) * mm});
            skLineSegment(sketch, "E19.77.0", {"start": v(46.29, -36.18) * mm, "end": v(47.52, -38.24) * mm});
            skLineSegment(sketch, "E19.77.1", {"start": v(47.52, -38.24) * mm, "end": v(47.4, -38.39) * mm});
            skLineSegment(sketch, "E19.77.2", {"start": v(47.29, -38.53) * mm, "end": v(47.4, -38.39) * mm});
            skLineSegment(sketch, "E19.77.3", {"start": v(45.02, -37.75) * mm, "end": v(47.29, -38.53) * mm});
            skLineSegment(sketch, "E19.78.0", {"start": v(48.12, -33.71) * mm, "end": v(49.46, -35.7) * mm});
            skLineSegment(sketch, "E19.78.1", {"start": v(49.46, -35.7) * mm, "end": v(49.35, -35.85) * mm});
            skLineSegment(sketch, "E19.78.2", {"start": v(49.24, -36) * mm, "end": v(49.35, -35.85) * mm});
            skLineSegment(sketch, "E19.78.3", {"start": v(46.93, -35.34) * mm, "end": v(49.24, -36) * mm});
            skLineSegment(sketch, "E19.79.0", {"start": v(49.81, -31.15) * mm, "end": v(51.26, -33.07) * mm});
            skLineSegment(sketch, "E19.79.1", {"start": v(51.26, -33.07) * mm, "end": v(51.16, -33.22) * mm});
            skLineSegment(sketch, "E19.79.2", {"start": v(51.06, -33.38) * mm, "end": v(51.16, -33.22) * mm});
            skLineSegment(sketch, "E19.79.3", {"start": v(48.71, -32.84) * mm, "end": v(51.06, -33.38) * mm});
            skLineSegment(sketch, "E19.80.0", {"start": v(51.38, -28.5) * mm, "end": v(52.92, -30.34) * mm});
            skLineSegment(sketch, "E19.80.1", {"start": v(52.92, -30.34) * mm, "end": v(52.83, -30.5) * mm});
            skLineSegment(sketch, "E19.80.2", {"start": v(52.73, -30.66) * mm, "end": v(52.83, -30.5) * mm});
            skLineSegment(sketch, "E19.80.3", {"start": v(50.37, -30.24) * mm, "end": v(52.73, -30.66) * mm});
            skLineSegment(sketch, "E19.81.0", {"start": v(52.8, -25.77) * mm, "end": v(54.44, -27.53) * mm});
            skLineSegment(sketch, "E19.81.1", {"start": v(54.44, -27.53) * mm, "end": v(54.35, -27.7) * mm});
            skLineSegment(sketch, "E19.81.2", {"start": v(54.27, -27.86) * mm, "end": v(54.35, -27.7) * mm});
            skLineSegment(sketch, "E19.81.3", {"start": v(51.88, -27.57) * mm, "end": v(54.27, -27.86) * mm});
            skLineSegment(sketch, "E19.82.0", {"start": v(54.07, -22.97) * mm, "end": v(55.8, -24.64) * mm});
            skLineSegment(sketch, "E19.82.1", {"start": v(55.8, -24.64) * mm, "end": v(55.73, -24.81) * mm});
            skLineSegment(sketch, "E19.82.2", {"start": v(55.65, -24.98) * mm, "end": v(55.73, -24.81) * mm});
            skLineSegment(sketch, "E19.82.3", {"start": v(53.25, -24.81) * mm, "end": v(55.65, -24.98) * mm});
            skLineSegment(sketch, "E19.83.0", {"start": v(55.2, -20.1) * mm, "end": v(57.02, -21.69) * mm});
            skLineSegment(sketch, "E19.83.1", {"start": v(57.02, -21.69) * mm, "end": v(56.95, -21.86) * mm});
            skLineSegment(sketch, "E19.83.2", {"start": v(56.88, -22.04) * mm, "end": v(56.95, -21.86) * mm});
            skLineSegment(sketch, "E19.83.3", {"start": v(54.48, -22) * mm, "end": v(56.88, -22.04) * mm});
            skLineSegment(sketch, "E19.84.0", {"start": v(56.18, -17.2) * mm, "end": v(58.07, -18.67) * mm});
            skLineSegment(sketch, "E19.84.1", {"start": v(58.07, -18.67) * mm, "end": v(58.01, -18.85) * mm});
            skLineSegment(sketch, "E19.84.2", {"start": v(57.96, -19.03) * mm, "end": v(58.01, -18.85) * mm});
            skLineSegment(sketch, "E19.84.3", {"start": v(55.55, -19.11) * mm, "end": v(57.96, -19.03) * mm});
            skLineSegment(sketch, "E19.85.0", {"start": v(57, -14.23) * mm, "end": v(58.97, -15.6) * mm});
            skLineSegment(sketch, "E19.85.1", {"start": v(58.97, -15.6) * mm, "end": v(58.92, -15.79) * mm});
            skLineSegment(sketch, "E19.85.2", {"start": v(58.87, -15.97) * mm, "end": v(58.92, -15.79) * mm});
            skLineSegment(sketch, "E19.85.3", {"start": v(56.48, -16.18) * mm, "end": v(58.87, -15.97) * mm});
            skLineSegment(sketch, "E19.86.0", {"start": v(57.67, -11.23) * mm, "end": v(59.7, -12.5) * mm});
            skLineSegment(sketch, "E19.86.1", {"start": v(59.7, -12.5) * mm, "end": v(59.67, -12.68) * mm});
            skLineSegment(sketch, "E19.86.2", {"start": v(59.63, -12.87) * mm, "end": v(59.67, -12.68) * mm});
            skLineSegment(sketch, "E19.86.3", {"start": v(57.25, -13.2) * mm, "end": v(59.63, -12.87) * mm});
            skLineSegment(sketch, "E19.87.0", {"start": v(58.18, -8.2) * mm, "end": v(60.28, -9.36) * mm});
            skLineSegment(sketch, "E19.87.1", {"start": v(60.28, -9.36) * mm, "end": v(60.25, -9.54) * mm});
            skLineSegment(sketch, "E19.87.2", {"start": v(60.22, -9.73) * mm, "end": v(60.25, -9.54) * mm});
            skLineSegment(sketch, "E19.87.3", {"start": v(57.86, -10.19) * mm, "end": v(60.22, -9.73) * mm});
            skLineSegment(sketch, "E19.88.0", {"start": v(58.53, -5.14) * mm, "end": v(60.69, -6.19) * mm});
            skLineSegment(sketch, "E19.88.1", {"start": v(60.69, -6.19) * mm, "end": v(60.67, -6.38) * mm});
            skLineSegment(sketch, "E19.88.2", {"start": v(60.65, -6.56) * mm, "end": v(60.67, -6.38) * mm});
            skLineSegment(sketch, "E19.88.3", {"start": v(58.31, -7.14) * mm, "end": v(60.65, -6.56) * mm});
            skLineSegment(sketch, "E19.89.0", {"start": v(58.71, -2.07) * mm, "end": v(60.93, -3) * mm});
            skLineSegment(sketch, "E19.89.1", {"start": v(60.93, -3) * mm, "end": v(60.92, -3.2) * mm});
            skLineSegment(sketch, "E19.89.2", {"start": v(60.9, -3.38) * mm, "end": v(60.92, -3.2) * mm});
            skLineSegment(sketch, "E19.89.3", {"start": v(58.6, -4.08) * mm, "end": v(60.9, -3.38) * mm});
            skLineSegment(sketch, "E19.90.0", {"start": v(58.74, 1) * mm, "end": v(61, 0.19) * mm});
            skLineSegment(sketch, "E19.90.1", {"start": v(61, 0.19) * mm, "end": v(61, 0) * mm});
            skLineSegment(sketch, "E19.90.2", {"start": v(61, -0.19) * mm, "end": v(61, 0) * mm});
            skLineSegment(sketch, "E19.90.3", {"start": v(58.74, -1) * mm, "end": v(61, -0.19) * mm});
            skLineSegment(sketch, "E19.91.0", {"start": v(58.6, 4.08) * mm, "end": v(60.9, 3.38) * mm});
            skLineSegment(sketch, "E19.91.1", {"start": v(60.9, 3.38) * mm, "end": v(60.92, 3.2) * mm});
            skLineSegment(sketch, "E19.91.2", {"start": v(60.93, 3) * mm, "end": v(60.92, 3.2) * mm});
            skLineSegment(sketch, "E19.91.3", {"start": v(58.71, 2.07) * mm, "end": v(60.93, 3) * mm});
            skLineSegment(sketch, "E19.92.0", {"start": v(58.31, 7.14) * mm, "end": v(60.65, 6.56) * mm});
            skLineSegment(sketch, "E19.92.1", {"start": v(60.65, 6.56) * mm, "end": v(60.67, 6.38) * mm});
            skLineSegment(sketch, "E19.92.2", {"start": v(60.69, 6.19) * mm, "end": v(60.67, 6.38) * mm});
            skLineSegment(sketch, "E19.92.3", {"start": v(58.53, 5.14) * mm, "end": v(60.69, 6.19) * mm});
            skLineSegment(sketch, "E19.93.0", {"start": v(57.86, 10.19) * mm, "end": v(60.22, 9.73) * mm});
            skLineSegment(sketch, "E19.93.1", {"start": v(60.22, 9.73) * mm, "end": v(60.25, 9.54) * mm});
            skLineSegment(sketch, "E19.93.2", {"start": v(60.28, 9.36) * mm, "end": v(60.25, 9.54) * mm});
            skLineSegment(sketch, "E19.93.3", {"start": v(58.18, 8.2) * mm, "end": v(60.28, 9.36) * mm});
            skLineSegment(sketch, "E19.94.0", {"start": v(57.25, 13.2) * mm, "end": v(59.63, 12.87) * mm});
            skLineSegment(sketch, "E19.94.1", {"start": v(59.63, 12.87) * mm, "end": v(59.67, 12.68) * mm});
            skLineSegment(sketch, "E19.94.2", {"start": v(59.7, 12.5) * mm, "end": v(59.67, 12.68) * mm});
            skLineSegment(sketch, "E19.94.3", {"start": v(57.67, 11.23) * mm, "end": v(59.7, 12.5) * mm});
            skLineSegment(sketch, "E19.95.0", {"start": v(56.48, 16.18) * mm, "end": v(58.87, 15.97) * mm});
            skLineSegment(sketch, "E19.95.1", {"start": v(58.87, 15.97) * mm, "end": v(58.92, 15.79) * mm});
            skLineSegment(sketch, "E19.95.2", {"start": v(58.97, 15.6) * mm, "end": v(58.92, 15.79) * mm});
            skLineSegment(sketch, "E19.95.3", {"start": v(57, 14.23) * mm, "end": v(58.97, 15.6) * mm});
            skLineSegment(sketch, "E19.96.0", {"start": v(55.55, 19.11) * mm, "end": v(57.96, 19.03) * mm});
            skLineSegment(sketch, "E19.96.1", {"start": v(57.96, 19.03) * mm, "end": v(58.01, 18.85) * mm});
            skLineSegment(sketch, "E19.96.2", {"start": v(58.07, 18.67) * mm, "end": v(58.01, 18.85) * mm});
            skLineSegment(sketch, "E19.96.3", {"start": v(56.18, 17.2) * mm, "end": v(58.07, 18.67) * mm});
            skLineSegment(sketch, "E19.97.0", {"start": v(54.48, 22) * mm, "end": v(56.88, 22.04) * mm});
            skLineSegment(sketch, "E19.97.1", {"start": v(56.88, 22.04) * mm, "end": v(56.95, 21.86) * mm});
            skLineSegment(sketch, "E19.97.2", {"start": v(57.02, 21.69) * mm, "end": v(56.95, 21.86) * mm});
            skLineSegment(sketch, "E19.97.3", {"start": v(55.2, 20.1) * mm, "end": v(57.02, 21.69) * mm});
            skLineSegment(sketch, "E19.98.0", {"start": v(53.25, 24.81) * mm, "end": v(55.65, 24.98) * mm});
            skLineSegment(sketch, "E19.98.1", {"start": v(55.65, 24.98) * mm, "end": v(55.73, 24.81) * mm});
            skLineSegment(sketch, "E19.98.2", {"start": v(55.8, 24.64) * mm, "end": v(55.73, 24.81) * mm});
            skLineSegment(sketch, "E19.98.3", {"start": v(54.07, 22.97) * mm, "end": v(55.8, 24.64) * mm});
            skLineSegment(sketch, "E19.99.0", {"start": v(51.88, 27.57) * mm, "end": v(54.27, 27.86) * mm});
            skLineSegment(sketch, "E19.99.1", {"start": v(54.27, 27.86) * mm, "end": v(54.35, 27.7) * mm});
            skLineSegment(sketch, "E19.99.2", {"start": v(54.44, 27.53) * mm, "end": v(54.35, 27.7) * mm});
            skLineSegment(sketch, "E19.99.3", {"start": v(52.8, 25.77) * mm, "end": v(54.44, 27.53) * mm});
            skLineSegment(sketch, "E19.100.0", {"start": v(50.37, 30.24) * mm, "end": v(52.73, 30.66) * mm});
            skLineSegment(sketch, "E19.100.1", {"start": v(52.73, 30.66) * mm, "end": v(52.83, 30.5) * mm});
            skLineSegment(sketch, "E19.100.2", {"start": v(52.92, 30.34) * mm, "end": v(52.83, 30.5) * mm});
            skLineSegment(sketch, "E19.100.3", {"start": v(51.38, 28.5) * mm, "end": v(52.92, 30.34) * mm});
            skLineSegment(sketch, "E19.101.0", {"start": v(48.71, 32.84) * mm, "end": v(51.06, 33.38) * mm});
            skLineSegment(sketch, "E19.101.1", {"start": v(51.06, 33.38) * mm, "end": v(51.16, 33.22) * mm});
            skLineSegment(sketch, "E19.101.2", {"start": v(51.26, 33.07) * mm, "end": v(51.16, 33.22) * mm});
            skLineSegment(sketch, "E19.101.3", {"start": v(49.81, 31.15) * mm, "end": v(51.26, 33.07) * mm});
            skLineSegment(sketch, "E19.102.0", {"start": v(46.93, 35.34) * mm, "end": v(49.24, 36) * mm});
            skLineSegment(sketch, "E19.102.1", {"start": v(49.24, 36) * mm, "end": v(49.35, 35.85) * mm});
            skLineSegment(sketch, "E19.102.2", {"start": v(49.46, 35.7) * mm, "end": v(49.35, 35.85) * mm});
            skLineSegment(sketch, "E19.102.3", {"start": v(48.12, 33.71) * mm, "end": v(49.46, 35.7) * mm});
            skLineSegment(sketch, "E19.103.0", {"start": v(45.02, 37.75) * mm, "end": v(47.29, 38.53) * mm});
            skLineSegment(sketch, "E19.103.1", {"start": v(47.29, 38.53) * mm, "end": v(47.4, 38.39) * mm});
            skLineSegment(sketch, "E19.103.2", {"start": v(47.52, 38.24) * mm, "end": v(47.4, 38.39) * mm});
            skLineSegment(sketch, "E19.103.3", {"start": v(46.29, 36.18) * mm, "end": v(47.52, 38.24) * mm});
            skLineSegment(sketch, "E19.104.0", {"start": v(42.98, 40.06) * mm, "end": v(45.2, 40.96) * mm});
            skLineSegment(sketch, "E19.104.1", {"start": v(45.2, 40.96) * mm, "end": v(45.33, 40.82) * mm});
            skLineSegment(sketch, "E19.104.2", {"start": v(45.46, 40.68) * mm, "end": v(45.33, 40.82) * mm});
            skLineSegment(sketch, "E19.104.3", {"start": v(44.33, 38.56) * mm, "end": v(45.46, 40.68) * mm});
            skLineSegment(sketch, "E19.105.0", {"start": v(40.82, 42.25) * mm, "end": v(43, 43.27) * mm});
            skLineSegment(sketch, "E19.105.1", {"start": v(43, 43.27) * mm, "end": v(43.13, 43.13) * mm});
            skLineSegment(sketch, "E19.105.2", {"start": v(43.27, 43) * mm, "end": v(43.13, 43.13) * mm});
            skLineSegment(sketch, "E19.105.3", {"start": v(42.25, 40.82) * mm, "end": v(43.27, 43) * mm});
            skLineSegment(sketch, "E19.106.0", {"start": v(38.56, 44.33) * mm, "end": v(40.68, 45.46) * mm});
            skLineSegment(sketch, "E19.106.1", {"start": v(40.68, 45.46) * mm, "end": v(40.82, 45.33) * mm});
            skLineSegment(sketch, "E19.106.2", {"start": v(40.96, 45.2) * mm, "end": v(40.82, 45.33) * mm});
            skLineSegment(sketch, "E19.106.3", {"start": v(40.06, 42.98) * mm, "end": v(40.96, 45.2) * mm});
            skLineSegment(sketch, "E19.107.0", {"start": v(36.18, 46.29) * mm, "end": v(38.24, 47.52) * mm});
            skLineSegment(sketch, "E19.107.1", {"start": v(38.24, 47.52) * mm, "end": v(38.39, 47.4) * mm});
            skLineSegment(sketch, "E19.107.2", {"start": v(38.53, 47.29) * mm, "end": v(38.39, 47.4) * mm});
            skLineSegment(sketch, "E19.107.3", {"start": v(37.75, 45.02) * mm, "end": v(38.53, 47.29) * mm});
            skLineSegment(sketch, "E19.108.0", {"start": v(33.71, 48.12) * mm, "end": v(35.7, 49.46) * mm});
            skLineSegment(sketch, "E19.108.1", {"start": v(35.7, 49.46) * mm, "end": v(35.85, 49.35) * mm});
            skLineSegment(sketch, "E19.108.2", {"start": v(36, 49.24) * mm, "end": v(35.85, 49.35) * mm});
            skLineSegment(sketch, "E19.108.3", {"start": v(35.34, 46.93) * mm, "end": v(36, 49.24) * mm});
            skLineSegment(sketch, "E19.109.0", {"start": v(31.15, 49.81) * mm, "end": v(33.07, 51.26) * mm});
            skLineSegment(sketch, "E19.109.1", {"start": v(33.07, 51.26) * mm, "end": v(33.22, 51.16) * mm});
            skLineSegment(sketch, "E19.109.2", {"start": v(33.38, 51.06) * mm, "end": v(33.22, 51.16) * mm});
            skLineSegment(sketch, "E19.109.3", {"start": v(32.84, 48.71) * mm, "end": v(33.38, 51.06) * mm});
            skLineSegment(sketch, "E19.110.0", {"start": v(28.5, 51.38) * mm, "end": v(30.34, 52.92) * mm});
            skLineSegment(sketch, "E19.110.1", {"start": v(30.34, 52.92) * mm, "end": v(30.5, 52.83) * mm});
            skLineSegment(sketch, "E19.110.2", {"start": v(30.66, 52.73) * mm, "end": v(30.5, 52.83) * mm});
            skLineSegment(sketch, "E19.110.3", {"start": v(30.24, 50.37) * mm, "end": v(30.66, 52.73) * mm});
            skLineSegment(sketch, "E19.111.0", {"start": v(25.77, 52.8) * mm, "end": v(27.53, 54.44) * mm});
            skLineSegment(sketch, "E19.111.1", {"start": v(27.53, 54.44) * mm, "end": v(27.7, 54.35) * mm});
            skLineSegment(sketch, "E19.111.2", {"start": v(27.86, 54.27) * mm, "end": v(27.7, 54.35) * mm});
            skLineSegment(sketch, "E19.111.3", {"start": v(27.57, 51.88) * mm, "end": v(27.86, 54.27) * mm});
            skLineSegment(sketch, "E19.112.0", {"start": v(22.97, 54.07) * mm, "end": v(24.64, 55.8) * mm});
            skLineSegment(sketch, "E19.112.1", {"start": v(24.64, 55.8) * mm, "end": v(24.81, 55.73) * mm});
            skLineSegment(sketch, "E19.112.2", {"start": v(24.98, 55.65) * mm, "end": v(24.81, 55.73) * mm});
            skLineSegment(sketch, "E19.112.3", {"start": v(24.81, 53.25) * mm, "end": v(24.98, 55.65) * mm});
            skLineSegment(sketch, "E19.113.0", {"start": v(20.1, 55.2) * mm, "end": v(21.69, 57.02) * mm});
            skLineSegment(sketch, "E19.113.1", {"start": v(21.69, 57.02) * mm, "end": v(21.86, 56.95) * mm});
            skLineSegment(sketch, "E19.113.2", {"start": v(22.04, 56.88) * mm, "end": v(21.86, 56.95) * mm});
            skLineSegment(sketch, "E19.113.3", {"start": v(22, 54.48) * mm, "end": v(22.04, 56.88) * mm});
            skLineSegment(sketch, "E19.114.0", {"start": v(17.2, 56.18) * mm, "end": v(18.67, 58.07) * mm});
            skLineSegment(sketch, "E19.114.1", {"start": v(18.67, 58.07) * mm, "end": v(18.85, 58.01) * mm});
            skLineSegment(sketch, "E19.114.2", {"start": v(19.03, 57.96) * mm, "end": v(18.85, 58.01) * mm});
            skLineSegment(sketch, "E19.114.3", {"start": v(19.11, 55.55) * mm, "end": v(19.03, 57.96) * mm});
            skLineSegment(sketch, "E19.115.0", {"start": v(14.23, 57) * mm, "end": v(15.6, 58.97) * mm});
            skLineSegment(sketch, "E19.115.1", {"start": v(15.6, 58.97) * mm, "end": v(15.79, 58.92) * mm});
            skLineSegment(sketch, "E19.115.2", {"start": v(15.97, 58.87) * mm, "end": v(15.79, 58.92) * mm});
            skLineSegment(sketch, "E19.115.3", {"start": v(16.18, 56.48) * mm, "end": v(15.97, 58.87) * mm});
            skLineSegment(sketch, "E19.116.0", {"start": v(11.23, 57.67) * mm, "end": v(12.5, 59.7) * mm});
            skLineSegment(sketch, "E19.116.1", {"start": v(12.5, 59.7) * mm, "end": v(12.68, 59.67) * mm});
            skLineSegment(sketch, "E19.116.2", {"start": v(12.87, 59.63) * mm, "end": v(12.68, 59.67) * mm});
            skLineSegment(sketch, "E19.116.3", {"start": v(13.2, 57.25) * mm, "end": v(12.87, 59.63) * mm});
            skLineSegment(sketch, "E19.117.0", {"start": v(8.2, 58.18) * mm, "end": v(9.36, 60.28) * mm});
            skLineSegment(sketch, "E19.117.1", {"start": v(9.36, 60.28) * mm, "end": v(9.54, 60.25) * mm});
            skLineSegment(sketch, "E19.117.2", {"start": v(9.73, 60.22) * mm, "end": v(9.54, 60.25) * mm});
            skLineSegment(sketch, "E19.117.3", {"start": v(10.19, 57.86) * mm, "end": v(9.73, 60.22) * mm});
            skLineSegment(sketch, "E19.118.0", {"start": v(5.14, 58.53) * mm, "end": v(6.19, 60.69) * mm});
            skLineSegment(sketch, "E19.118.1", {"start": v(6.19, 60.69) * mm, "end": v(6.38, 60.67) * mm});
            skLineSegment(sketch, "E19.118.2", {"start": v(6.56, 60.65) * mm, "end": v(6.38, 60.67) * mm});
            skLineSegment(sketch, "E19.118.3", {"start": v(7.14, 58.31) * mm, "end": v(6.56, 60.65) * mm});
            skLineSegment(sketch, "E19.119.0", {"start": v(2.07, 58.71) * mm, "end": v(3, 60.93) * mm});
            skLineSegment(sketch, "E19.119.1", {"start": v(3, 60.93) * mm, "end": v(3.2, 60.92) * mm});
            skLineSegment(sketch, "E19.119.2", {"start": v(3.38, 60.9) * mm, "end": v(3.2, 60.92) * mm});
            skLineSegment(sketch, "E19.119.3", {"start": v(4.08, 58.6) * mm, "end": v(3.38, 60.9) * mm});
            skCircle(sketch, "E20", {"center": v(0, 0) * mm, "radius": 7.5 * mm});
            skSolve(sketch);
        }
        {
            var Q0;
            Q0 = qSketchRegion(id + "F4", true);
            extrude(context, id + "F5", {"entities" : qUnion([Q0]), "operationType" : NewBodyOperationType.ADD, "depth" : 10 * mm});
        }
        {
            var Q0;
            Q0=makeQuery(id+"F3.opExtrude","SWEPT_FACE",FACE,{"disambiguationData":[OSD([sQuery(id+"F2.wireOp",EDGE,"E11.top")])]});
            var sketch = newSketch(context, id + "F6", { "sketchPlane" : qUnion([Q0])});
            skLineSegment(sketch, "E21", {"start": v(0, 10) * mm, "end": v(0, 5) * mm, "construction": true});
            skPoint(sketch, "E21.endSnap0", {"position": v(-15, 5) * mm});
            skCircle(sketch, "E22", {"center": v(0, 5) * mm, "radius": 0.5 * mm});
            skSolve(sketch);
        }
        {
            var Q0;
            Q0 = qSketchRegion(id + "F6", true);
            extrude(context, id + "F7", {"entities" : qUnion([Q0]), "operationType" : NewBodyOperationType.REMOVE, "depth" : -1 * mm});
        }
    });
